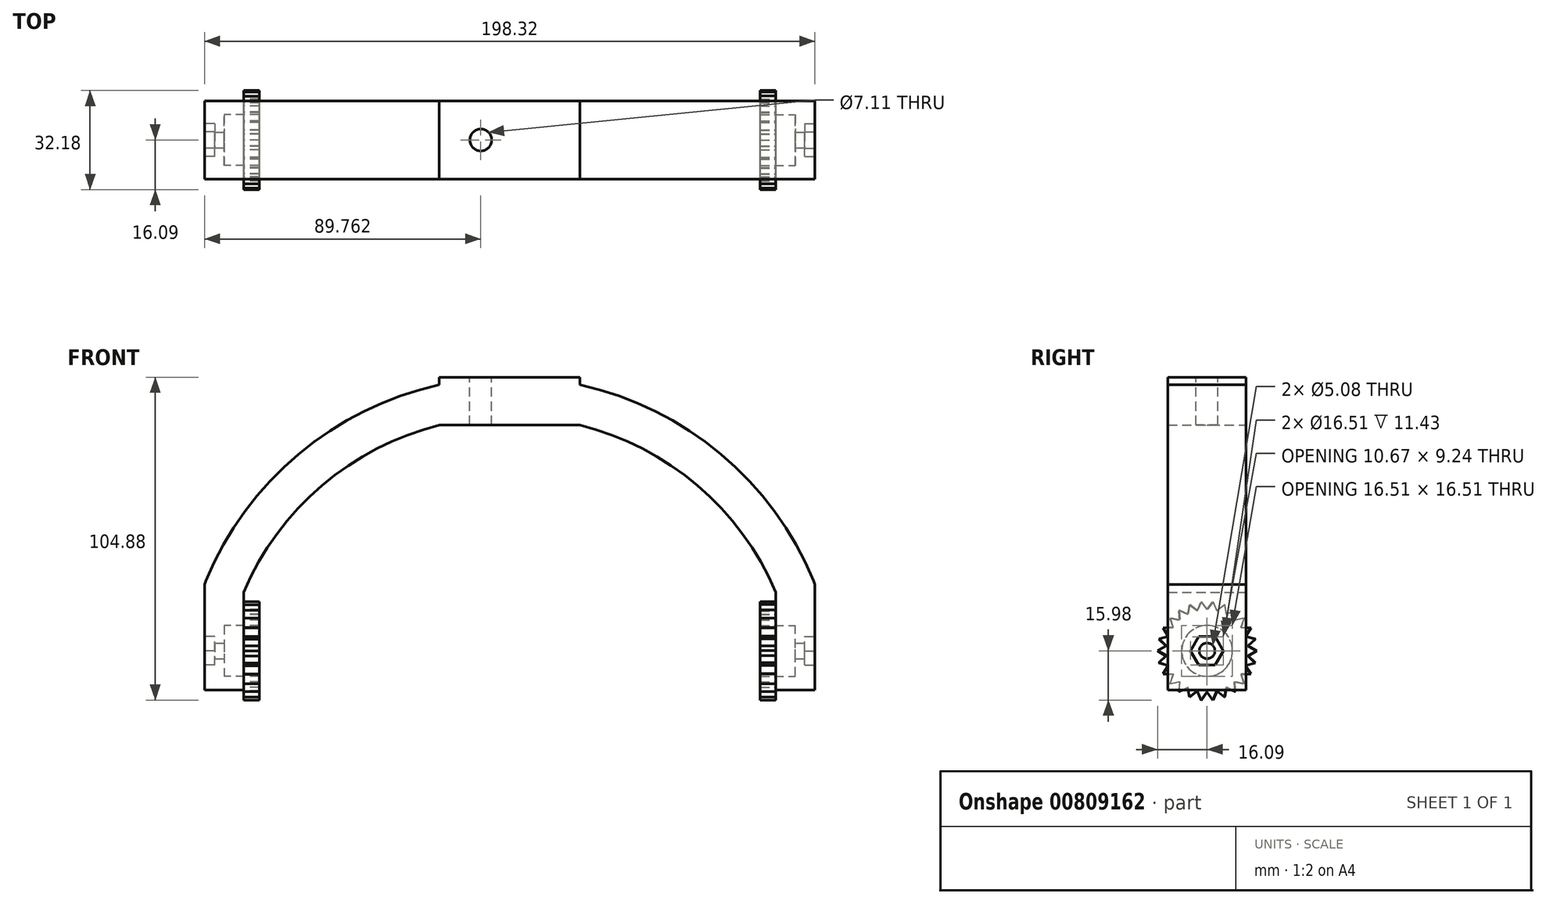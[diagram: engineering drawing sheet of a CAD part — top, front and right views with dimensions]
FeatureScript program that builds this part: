
annotation { "Feature Type Name" : "Feature", "Feature Type Description" : "" }
export const myFeature = defineFeature(function(context is Context, id is Id, definition is map)
    precondition{}
    {
        {
            var Q0;
            Q0=qCreatedBy(makeId("Front.planeOp"),FACE);
            var sketch = newSketch(context, id + "F0", { "sketchPlane" : qUnion([Q0])});
            skArc(sketch, "E0", {"start": v(92.81, 33.02) * mm, "mid": v(0, 95.25) * mm, "end": v(-92.81, 33.02) * mm});
            skLineSegment(sketch, "E1", {"start": v(-92.81, 33.02) * mm, "end": v(-92.81, 0) * mm});
            skLineSegment(sketch, "E2", {"start": v(92.81, 33.02) * mm, "end": v(92.81, 0) * mm});
            skLineSegment(sketch, "E3", {"start": v(0, 0) * mm, "end": v(0, 95.25) * mm, "construction": true});
            skSolve(sketch);
        }
        {
            var Q0;
            Q0=qCreatedBy(makeId("Top.planeOp"),FACE);
            var sketch = newSketch(context, id + "F1", { "sketchPlane" : qUnion([Q0])});
            skPoint(sketch, "E4.0", {"position": v(-92.81, 0) * mm});
            skLineSegment(sketch, "E5.bottom", {"start": v(-99.16, 12.7) * mm, "end": v(-86.46, 12.7) * mm});
            skLineSegment(sketch, "E5.top", {"start": v(-99.16, -12.7) * mm, "end": v(-86.46, -12.7) * mm});
            skLineSegment(sketch, "E5.left", {"start": v(-99.16, 12.7) * mm, "end": v(-99.16, -12.7) * mm});
            skLineSegment(sketch, "E5.right", {"start": v(-86.46, 12.7) * mm, "end": v(-86.46, -12.7) * mm});
            skSolve(sketch);
        }
        {
            var Q0;
            Q0=qSketchRegion(id+"F1",true);
            var Q1;
            Q1=qConstructionFilter(qBodyType(qCreatedBy(id+"F0",EDGE),BodyType.WIRE),ConstructionObject.NO);
            sweep(context, id + "F2", {"profiles" : qUnion([Q0]), "path" : qUnion([Q1])});
        }
        {
            var Q0;
            Q0=qCreatedBy(makeId("Right.planeOp"),FACE);
            var sketch = newSketch(context, id + "F3", { "sketchPlane" : qUnion([Q0])});
            skCircle(sketch, "E6", {"center": v(0, 12.7) * mm, "radius": 2.54 * mm});
            skSolve(sketch);
        }
        {
            var Q0;
            Q0=qSketchRegion(id+"F3",true);
            extrude(context, id + "F4", {"entities" : qUnion([Q0]), "operationType" : NewBodyOperationType.REMOVE, "endBound" : BoundingType.SYMMETRIC, "oppositeDirection" : true, "depth" : 254 * mm, "offsetDistance" : 25.4 * mm});
        }
        {
            var Q0;
            Q0=makeQuery(id+"F2.opSweep","SWEPT_FACE",FACE,{"disambiguationData":[OSD([sQuery(id+"F0.wireOp",EDGE,"E2"),sQuery(id+"F1.wireOp",EDGE,"E5.left")])]});
            var Q1;
            Q1=makeQuery(id+"F2.opSweep","CAP_VERTEX",VERTEX,{"disambiguationData":[OSD([sQuery(id+"F0.wireOp",EDGE,"E2"),sQuery(id+"F1.wireOp",EDGE,"E5.bottom"),sQuery(id+"F1.wireOp",EDGE,"E5.left")])],"isStart":false});
            cPlane(context, id + "F5", {"entities" : qUnion([Q0, Q1]), "cplaneType" : CPlaneType.PLANE_POINT, "offset" : 25.4 * mm, "width" : 152.4 * mm, "height" : 152.4 * mm});
        }
        {
            var Q0;
            Q0=qCreatedBy(id+"F5.planeOp",FACE);
            var sketch = newSketch(context, id + "F6", { "sketchPlane" : qUnion([Q0])});
            skCircle(sketch, "E7", {"center": v(0, 12.7) * mm, "radius": 5.33 * mm, "construction": true});
            skLineSegment(sketch, "E8.0", {"start": v(-2.67, 17.32) * mm, "end": v(2.67, 17.32) * mm});
            skLineSegment(sketch, "E8.1", {"start": v(2.67, 17.32) * mm, "end": v(5.33, 12.7) * mm});
            skLineSegment(sketch, "E8.2", {"start": v(5.33, 12.7) * mm, "end": v(2.67, 8.08) * mm});
            skLineSegment(sketch, "E8.3", {"start": v(2.67, 8.08) * mm, "end": v(-2.67, 8.08) * mm});
            skLineSegment(sketch, "E8.4", {"start": v(-2.67, 8.08) * mm, "end": v(-5.33, 12.7) * mm});
            skLineSegment(sketch, "E8.5", {"start": v(-5.33, 12.7) * mm, "end": v(-2.67, 17.32) * mm});
            skSolve(sketch);
        }
        {
            var Q0;
            Q0=makeQuery(id+"F6.imprint","IMPRINT",FACE,{"disambiguationData":[TD([[makeQuery(id+"F6.imprint","IMPRINT",EDGE,{"derivedFrom":sQuery(id+"F6.wireOp",EDGE,"E8.0")}),-1.0]])]});
            extrude(context, id + "F7", {"entities" : qUnion([Q0]), "operationType" : NewBodyOperationType.REMOVE, "oppositeDirection" : true, "depth" : 3.3 * mm, "offsetDistance" : 25.4 * mm});
        }
        {
            var Q0;
            Q0=makeQuery(id+"F2.opSweep","SWEPT_FACE",FACE,{"disambiguationData":[OSD([sQuery(id+"F0.wireOp",EDGE,"E1"),sQuery(id+"F1.wireOp",EDGE,"E5.left")])]});
            var Q1;
            Q1=makeQuery(id+"F2.opSweep","CAP_VERTEX",VERTEX,{"disambiguationData":[OSD([sQuery(id+"F0.wireOp",EDGE,"E1"),sQuery(id+"F1.wireOp",EDGE,"E5.bottom"),sQuery(id+"F1.wireOp",EDGE,"E5.left")])],"isStart":true});
            cPlane(context, id + "F8", {"entities" : qUnion([Q0, Q1]), "cplaneType" : CPlaneType.PLANE_POINT, "offset" : 25.4 * mm, "width" : 152.4 * mm, "height" : 152.4 * mm});
        }
        {
            var Q0;
            Q0=qCreatedBy(id+"F8.planeOp",FACE);
            var sketch = newSketch(context, id + "F9", { "sketchPlane" : qUnion([Q0])});
            skLineSegment(sketch, "E9", {"start": v(0, 0) * mm, "end": v(0, 12.7) * mm, "construction": true});
            skCircle(sketch, "E10", {"center": v(0, 12.7) * mm, "radius": 5.33 * mm, "construction": true});
            skLineSegment(sketch, "E11.0", {"start": v(-2.67, 17.32) * mm, "end": v(2.67, 17.32) * mm});
            skLineSegment(sketch, "E11.1", {"start": v(2.67, 17.32) * mm, "end": v(5.33, 12.7) * mm});
            skLineSegment(sketch, "E11.2", {"start": v(5.33, 12.7) * mm, "end": v(2.67, 8.08) * mm});
            skLineSegment(sketch, "E11.3", {"start": v(2.67, 8.08) * mm, "end": v(-2.67, 8.08) * mm});
            skLineSegment(sketch, "E11.4", {"start": v(-2.67, 8.08) * mm, "end": v(-5.33, 12.7) * mm});
            skLineSegment(sketch, "E11.5", {"start": v(-5.33, 12.7) * mm, "end": v(-2.67, 17.32) * mm});
            skSolve(sketch);
        }
        {
            var Q0;
            Q0=makeQuery(id+"F9.imprint","IMPRINT",FACE,{"disambiguationData":[TD([[makeQuery(id+"F9.imprint","IMPRINT",EDGE,{"derivedFrom":sQuery(id+"F9.wireOp",EDGE,"E11.0")}),-1.0]])]});
            extrude(context, id + "F10", {"entities" : qUnion([Q0]), "operationType" : NewBodyOperationType.REMOVE, "oppositeDirection" : true, "depth" : 3.3 * mm, "offsetDistance" : 25.4 * mm});
        }
        {
            var Q0;
            Q0=makeQuery(id+"F2.opSweep","SWEPT_FACE",FACE,{"disambiguationData":[OSD([sQuery(id+"F0.wireOp",EDGE,"E1"),sQuery(id+"F1.wireOp",EDGE,"E5.left")])]});
            cPlane(context, id + "F11", {"entities" : qUnion([Q0]), "cplaneType" : CPlaneType.OFFSET, "offset" : 6.35 * mm, "oppositeDirection" : true, "width" : 152.4 * mm, "height" : 152.4 * mm});
        }
        {
            var Q0;
            Q0=qCreatedBy(id+"F11.planeOp",FACE);
            var sketch = newSketch(context, id + "F12", { "sketchPlane" : qUnion([Q0])});
            skLineSegment(sketch, "E12", {"start": v(0, 0) * mm, "end": v(0, 12.7) * mm, "construction": true});
            skCircle(sketch, "E13", {"center": v(0, 12.7) * mm, "radius": 8.26 * mm});
            skSolve(sketch);
        }
        {
            var Q0;
            Q0=makeQuery(id+"F2.opSweep","SWEPT_FACE",FACE,{"disambiguationData":[OSD([sQuery(id+"F0.wireOp",EDGE,"E2"),sQuery(id+"F1.wireOp",EDGE,"E5.left")])]});
            cPlane(context, id + "F13", {"entities" : qUnion([Q0]), "cplaneType" : CPlaneType.OFFSET, "offset" : 6.35 * mm, "oppositeDirection" : true, "width" : 152.4 * mm, "height" : 152.4 * mm});
        }
        {
            var Q0;
            Q0=qCreatedBy(id+"F13.planeOp",FACE);
            var sketch = newSketch(context, id + "F14", { "sketchPlane" : qUnion([Q0])});
            skLineSegment(sketch, "E14", {"start": v(0, 0) * mm, "end": v(0, 12.7) * mm, "construction": true});
            skCircle(sketch, "E15", {"center": v(0, 12.7) * mm, "radius": 8.26 * mm});
            skSolve(sketch);
        }
        {
            var Q0;
            Q0=makeQuery(id+"F2.opSweep","SWEPT_FACE",FACE,{"disambiguationData":[OSD([sQuery(id+"F0.wireOp",EDGE,"E1"),sQuery(id+"F1.wireOp",EDGE,"E5.right")])]});
            var sketch = newSketch(context, id + "F15", { "sketchPlane" : qUnion([Q0])});
            skCircle(sketch, "E16", {"center": v(0, 12.7) * mm, "radius": 13.34 * mm, "construction": true});
            skLineSegment(sketch, "E17", {"start": v(-3.28, 25.63) * mm, "end": v(-2, 28.67) * mm});
            skLineSegment(sketch, "E18", {"start": v(-2, 28.67) * mm, "end": v(0, 26.04) * mm});
            skLineSegment(sketch, "E19.1.0", {"start": v(-6.27, 24.47) * mm, "end": v(-5.76, 27.73) * mm});
            skLineSegment(sketch, "E19.1.1", {"start": v(-5.76, 27.73) * mm, "end": v(-3.2, 25.65) * mm});
            skLineSegment(sketch, "E19.2.0", {"start": v(-8.9, 22.62) * mm, "end": v(-9.18, 25.91) * mm});
            skLineSegment(sketch, "E19.2.1", {"start": v(-9.18, 25.91) * mm, "end": v(-6.2, 24.5) * mm});
            skLineSegment(sketch, "E19.3.0", {"start": v(-11.02, 20.2) * mm, "end": v(-12.08, 23.33) * mm});
            skLineSegment(sketch, "E19.3.1", {"start": v(-12.08, 23.33) * mm, "end": v(-8.84, 22.68) * mm});
            skLineSegment(sketch, "E19.4.0", {"start": v(-12.5, 17.35) * mm, "end": v(-14.27, 20.13) * mm});
            skLineSegment(sketch, "E19.4.1", {"start": v(-14.27, 20.13) * mm, "end": v(-10.97, 20.28) * mm});
            skLineSegment(sketch, "E19.5.0", {"start": v(-13.25, 14.22) * mm, "end": v(-15.64, 16.5) * mm});
            skLineSegment(sketch, "E19.5.1", {"start": v(-15.64, 16.5) * mm, "end": v(-12.47, 17.43) * mm});
            skLineSegment(sketch, "E19.6.0", {"start": v(-13.23, 11) * mm, "end": v(-16.1, 12.65) * mm});
            skLineSegment(sketch, "E19.6.1", {"start": v(-16.1, 12.65) * mm, "end": v(-13.24, 14.3) * mm});
            skLineSegment(sketch, "E19.7.0", {"start": v(-12.44, 7.89) * mm, "end": v(-15.61, 8.8) * mm});
            skLineSegment(sketch, "E19.7.1", {"start": v(-15.61, 8.8) * mm, "end": v(-13.24, 11.1) * mm});
            skLineSegment(sketch, "E19.8.0", {"start": v(-10.92, 5.05) * mm, "end": v(-14.22, 5.17) * mm});
            skLineSegment(sketch, "E19.8.1", {"start": v(-14.22, 5.17) * mm, "end": v(-12.47, 7.97) * mm});
            skLineSegment(sketch, "E19.9.0", {"start": v(-8.78, 2.66) * mm, "end": v(-12, 1.99) * mm});
            skLineSegment(sketch, "E19.9.1", {"start": v(-12, 1.99) * mm, "end": v(-10.97, 5.12) * mm});
            skLineSegment(sketch, "E19.10.0", {"start": v(-6.12, 0.85) * mm, "end": v(-9.1, -0.57) * mm});
            skLineSegment(sketch, "E19.10.1", {"start": v(-9.1, -0.57) * mm, "end": v(-8.84, 2.72) * mm});
            skLineSegment(sketch, "E19.11.0", {"start": v(-3.1, -0.27) * mm, "end": v(-5.66, -2.37) * mm});
            skLineSegment(sketch, "E19.11.1", {"start": v(-5.66, -2.37) * mm, "end": v(-6.2, 0.9) * mm});
            skLineSegment(sketch, "E19.12.0", {"start": v(0.09, -0.63) * mm, "end": v(-1.89, -3.28) * mm});
            skLineSegment(sketch, "E19.12.1", {"start": v(-1.89, -3.28) * mm, "end": v(-3.2, -0.25) * mm});
            skLineSegment(sketch, "E19.13.0", {"start": v(3.28, -0.23) * mm, "end": v(2, -3.27) * mm});
            skLineSegment(sketch, "E19.13.1", {"start": v(2, -3.27) * mm, "end": v(0, -0.63) * mm});
            skLineSegment(sketch, "E19.14.0", {"start": v(6.27, 0.93) * mm, "end": v(5.76, -2.33) * mm});
            skLineSegment(sketch, "E19.14.1", {"start": v(5.76, -2.33) * mm, "end": v(3.2, -0.25) * mm});
            skLineSegment(sketch, "E19.15.0", {"start": v(8.9, 2.78) * mm, "end": v(9.18, -0.51) * mm});
            skLineSegment(sketch, "E19.15.1", {"start": v(9.18, -0.51) * mm, "end": v(6.2, 0.9) * mm});
            skLineSegment(sketch, "E19.16.0", {"start": v(11.02, 5.2) * mm, "end": v(12.08, 2.07) * mm});
            skLineSegment(sketch, "E19.16.1", {"start": v(12.08, 2.07) * mm, "end": v(8.84, 2.72) * mm});
            skLineSegment(sketch, "E19.17.0", {"start": v(12.5, 8.05) * mm, "end": v(14.27, 5.27) * mm});
            skLineSegment(sketch, "E19.17.1", {"start": v(14.27, 5.27) * mm, "end": v(10.97, 5.12) * mm});
            skLineSegment(sketch, "E19.18.0", {"start": v(13.25, 11.18) * mm, "end": v(15.64, 8.9) * mm});
            skLineSegment(sketch, "E19.18.1", {"start": v(15.64, 8.9) * mm, "end": v(12.47, 7.97) * mm});
            skLineSegment(sketch, "E19.19.0", {"start": v(13.23, 14.4) * mm, "end": v(16.1, 12.75) * mm});
            skLineSegment(sketch, "E19.19.1", {"start": v(16.1, 12.75) * mm, "end": v(13.24, 11.1) * mm});
            skLineSegment(sketch, "E19.20.0", {"start": v(12.44, 17.51) * mm, "end": v(15.61, 16.6) * mm});
            skLineSegment(sketch, "E19.20.1", {"start": v(15.61, 16.6) * mm, "end": v(13.24, 14.3) * mm});
            skLineSegment(sketch, "E19.21.0", {"start": v(10.92, 20.35) * mm, "end": v(14.22, 20.23) * mm});
            skLineSegment(sketch, "E19.21.1", {"start": v(14.22, 20.23) * mm, "end": v(12.47, 17.43) * mm});
            skLineSegment(sketch, "E19.22.0", {"start": v(8.78, 22.74) * mm, "end": v(12, 23.41) * mm});
            skLineSegment(sketch, "E19.22.1", {"start": v(12, 23.41) * mm, "end": v(10.97, 20.28) * mm});
            skLineSegment(sketch, "E19.23.0", {"start": v(6.12, 24.55) * mm, "end": v(9.1, 25.97) * mm});
            skLineSegment(sketch, "E19.23.1", {"start": v(9.1, 25.97) * mm, "end": v(8.84, 22.68) * mm});
            skLineSegment(sketch, "E19.24.0", {"start": v(3.1, 25.67) * mm, "end": v(5.66, 27.77) * mm});
            skLineSegment(sketch, "E19.24.1", {"start": v(5.66, 27.77) * mm, "end": v(6.2, 24.5) * mm});
            skLineSegment(sketch, "E19.25.0", {"start": v(-0.09, 26.03) * mm, "end": v(1.89, 28.68) * mm});
            skLineSegment(sketch, "E19.25.1", {"start": v(1.89, 28.68) * mm, "end": v(3.2, 25.65) * mm});
            skSolve(sketch);
        }
        {
            var Q0;
            Q0=qSketchRegion(id+"F15",true);
            extrude(context, id + "F16", {"entities" : qUnion([Q0]), "operationType" : NewBodyOperationType.ADD, "depth" : 5.08 * mm, "offsetDistance" : 25.4 * mm});
        }
        {
            var Q0;
            Q0=makeQuery(id+"F2.opSweep","SWEPT_FACE",FACE,{"disambiguationData":[OSD([sQuery(id+"F0.wireOp",EDGE,"E2"),sQuery(id+"F1.wireOp",EDGE,"E5.right")])]});
            var sketch = newSketch(context, id + "F17", { "sketchPlane" : qUnion([Q0])});
            skCircle(sketch, "E20", {"center": v(0, 12.7) * mm, "radius": 13.34 * mm, "construction": true});
            skLineSegment(sketch, "E21", {"start": v(-3.28, 25.63) * mm, "end": v(-2, 28.67) * mm});
            skLineSegment(sketch, "E22", {"start": v(-2, 28.67) * mm, "end": v(0, 26.04) * mm});
            skLineSegment(sketch, "E23.1.0", {"start": v(-5.76, 27.73) * mm, "end": v(-3.2, 25.65) * mm});
            skLineSegment(sketch, "E23.1.1", {"start": v(-6.27, 24.47) * mm, "end": v(-5.76, 27.73) * mm});
            skLineSegment(sketch, "E23.2.0", {"start": v(-9.18, 25.91) * mm, "end": v(-6.2, 24.5) * mm});
            skLineSegment(sketch, "E23.2.1", {"start": v(-8.9, 22.62) * mm, "end": v(-9.18, 25.91) * mm});
            skLineSegment(sketch, "E23.3.0", {"start": v(-12.08, 23.33) * mm, "end": v(-8.84, 22.68) * mm});
            skLineSegment(sketch, "E23.3.1", {"start": v(-11.02, 20.2) * mm, "end": v(-12.08, 23.33) * mm});
            skLineSegment(sketch, "E23.4.0", {"start": v(-14.27, 20.13) * mm, "end": v(-10.97, 20.28) * mm});
            skLineSegment(sketch, "E23.4.1", {"start": v(-12.5, 17.35) * mm, "end": v(-14.27, 20.13) * mm});
            skLineSegment(sketch, "E23.5.0", {"start": v(-15.64, 16.5) * mm, "end": v(-12.47, 17.43) * mm});
            skLineSegment(sketch, "E23.5.1", {"start": v(-13.25, 14.22) * mm, "end": v(-15.64, 16.5) * mm});
            skLineSegment(sketch, "E23.6.0", {"start": v(-16.1, 12.65) * mm, "end": v(-13.24, 14.3) * mm});
            skLineSegment(sketch, "E23.6.1", {"start": v(-13.23, 11) * mm, "end": v(-16.1, 12.65) * mm});
            skLineSegment(sketch, "E23.7.0", {"start": v(-15.61, 8.8) * mm, "end": v(-13.24, 11.1) * mm});
            skLineSegment(sketch, "E23.7.1", {"start": v(-12.44, 7.89) * mm, "end": v(-15.61, 8.8) * mm});
            skLineSegment(sketch, "E23.8.0", {"start": v(-14.22, 5.17) * mm, "end": v(-12.47, 7.97) * mm});
            skLineSegment(sketch, "E23.8.1", {"start": v(-10.92, 5.05) * mm, "end": v(-14.22, 5.17) * mm});
            skLineSegment(sketch, "E23.9.0", {"start": v(-12, 1.99) * mm, "end": v(-10.97, 5.12) * mm});
            skLineSegment(sketch, "E23.9.1", {"start": v(-8.78, 2.66) * mm, "end": v(-12, 1.99) * mm});
            skLineSegment(sketch, "E23.10.0", {"start": v(-9.1, -0.57) * mm, "end": v(-8.84, 2.72) * mm});
            skLineSegment(sketch, "E23.10.1", {"start": v(-6.12, 0.85) * mm, "end": v(-9.1, -0.57) * mm});
            skLineSegment(sketch, "E23.11.0", {"start": v(-5.66, -2.37) * mm, "end": v(-6.2, 0.9) * mm});
            skLineSegment(sketch, "E23.11.1", {"start": v(-3.1, -0.27) * mm, "end": v(-5.66, -2.37) * mm});
            skLineSegment(sketch, "E23.12.0", {"start": v(-1.89, -3.28) * mm, "end": v(-3.2, -0.25) * mm});
            skLineSegment(sketch, "E23.12.1", {"start": v(0.09, -0.63) * mm, "end": v(-1.89, -3.28) * mm});
            skLineSegment(sketch, "E23.13.0", {"start": v(2, -3.27) * mm, "end": v(0, -0.63) * mm});
            skLineSegment(sketch, "E23.13.1", {"start": v(3.28, -0.23) * mm, "end": v(2, -3.27) * mm});
            skLineSegment(sketch, "E23.14.0", {"start": v(5.76, -2.33) * mm, "end": v(3.2, -0.25) * mm});
            skLineSegment(sketch, "E23.14.1", {"start": v(6.27, 0.93) * mm, "end": v(5.76, -2.33) * mm});
            skLineSegment(sketch, "E23.15.0", {"start": v(9.18, -0.51) * mm, "end": v(6.2, 0.9) * mm});
            skLineSegment(sketch, "E23.15.1", {"start": v(8.9, 2.78) * mm, "end": v(9.18, -0.51) * mm});
            skLineSegment(sketch, "E23.16.0", {"start": v(12.08, 2.07) * mm, "end": v(8.84, 2.72) * mm});
            skLineSegment(sketch, "E23.16.1", {"start": v(11.02, 5.2) * mm, "end": v(12.08, 2.07) * mm});
            skLineSegment(sketch, "E23.17.0", {"start": v(14.27, 5.27) * mm, "end": v(10.97, 5.12) * mm});
            skLineSegment(sketch, "E23.17.1", {"start": v(12.5, 8.05) * mm, "end": v(14.27, 5.27) * mm});
            skLineSegment(sketch, "E23.18.0", {"start": v(15.64, 8.9) * mm, "end": v(12.47, 7.97) * mm});
            skLineSegment(sketch, "E23.18.1", {"start": v(13.25, 11.18) * mm, "end": v(15.64, 8.9) * mm});
            skLineSegment(sketch, "E23.19.0", {"start": v(16.1, 12.75) * mm, "end": v(13.24, 11.1) * mm});
            skLineSegment(sketch, "E23.19.1", {"start": v(13.23, 14.4) * mm, "end": v(16.1, 12.75) * mm});
            skLineSegment(sketch, "E23.20.0", {"start": v(15.61, 16.6) * mm, "end": v(13.24, 14.3) * mm});
            skLineSegment(sketch, "E23.20.1", {"start": v(12.44, 17.51) * mm, "end": v(15.61, 16.6) * mm});
            skLineSegment(sketch, "E23.21.0", {"start": v(14.22, 20.23) * mm, "end": v(12.47, 17.43) * mm});
            skLineSegment(sketch, "E23.21.1", {"start": v(10.92, 20.35) * mm, "end": v(14.22, 20.23) * mm});
            skLineSegment(sketch, "E23.22.0", {"start": v(12, 23.41) * mm, "end": v(10.97, 20.28) * mm});
            skLineSegment(sketch, "E23.22.1", {"start": v(8.78, 22.74) * mm, "end": v(12, 23.41) * mm});
            skLineSegment(sketch, "E23.23.0", {"start": v(9.1, 25.97) * mm, "end": v(8.84, 22.68) * mm});
            skLineSegment(sketch, "E23.23.1", {"start": v(6.12, 24.55) * mm, "end": v(9.1, 25.97) * mm});
            skLineSegment(sketch, "E23.24.0", {"start": v(5.66, 27.77) * mm, "end": v(6.2, 24.5) * mm});
            skLineSegment(sketch, "E23.24.1", {"start": v(3.1, 25.67) * mm, "end": v(5.66, 27.77) * mm});
            skLineSegment(sketch, "E23.25.0", {"start": v(1.89, 28.68) * mm, "end": v(3.2, 25.65) * mm});
            skLineSegment(sketch, "E23.25.1", {"start": v(-0.09, 26.03) * mm, "end": v(1.89, 28.68) * mm});
            skSolve(sketch);
        }
        {
            var Q0;
            Q0=qSketchRegion(id+"F17",true);
            var Q1;
            Q1=makeQuery(id+"F2.opSweep","SWEPT_FACE",FACE,{"disambiguationData":[OSD([sQuery(id+"F0.wireOp",EDGE,"E2"),sQuery(id+"F1.wireOp",EDGE,"E5.left")])]});
            extrude(context, id + "F18", {"entities" : qUnion([Q0, Q1]), "operationType" : NewBodyOperationType.ADD, "depth" : 5.08 * mm, "offsetDistance" : 25.4 * mm});
        }
        {
            var Q0;
            Q0=qSketchRegion(id+"F12",true);
            extrude(context, id + "F19", {"entities" : qUnion([Q0]), "operationType" : NewBodyOperationType.REMOVE, "oppositeDirection" : true, "depth" : 63.75 * mm, "offsetDistance" : 25.4 * mm});
        }
        {
            var Q0;
            Q0=qSketchRegion(id+"F14",true);
            extrude(context, id + "F20", {"entities" : qUnion([Q0]), "operationType" : NewBodyOperationType.REMOVE, "oppositeDirection" : true, "depth" : 25.4 * mm, "offsetDistance" : 25.4 * mm});
        }
        {
            var Q0;
            Q0=makeQuery(id+"F2.opSweep","SWEPT_EDGE",EDGE,{"disambiguationData":[OSD([sQuery(id+"F0.wireOp",EDGE,"E0"),sQuery(id+"F1.wireOp",EDGE,"E5.top"),sQuery(id+"F1.wireOp",EDGE,"E5.left")]),OD(2.0)]});
            cPoint(context, id + "F21", {"entities" : qUnion([Q0]), "parameter" : 0.5});
        }
        {
            var Q0;
            Q0=qCreatedBy(makeId("Top.planeOp"),FACE);
            var Q1;
            Q1=qCreatedBy(id+"F21",VERTEX);
            cPlane(context, id + "F22", {"entities" : qUnion([Q0, Q1]), "cplaneType" : CPlaneType.PLANE_POINT, "offset" : 25.4 * mm, "width" : 152.4 * mm, "height" : 152.4 * mm});
        }
        {
            var Q0;
            Q0=qCreatedBy(id+"F22.planeOp",FACE);
            var sketch = newSketch(context, id + "F23", { "sketchPlane" : qUnion([Q0])});
            skFitSpline(sketch, "E24.0", {"points": [v(-103.2, 12.7) * mm, v(-34.4, 12.7) * mm, v(34.4, 12.7) * mm, v(103.2, 12.7) * mm]});
            skLineSegment(sketch, "E25.bottom", {"start": v(-22.86, 12.7) * mm, "end": v(22.86, 12.7) * mm});
            skLineSegment(sketch, "E25.top", {"start": v(-22.86, -12.7) * mm, "end": v(22.86, -12.7) * mm});
            skLineSegment(sketch, "E25.left", {"start": v(-22.86, 12.7) * mm, "end": v(-22.86, -12.7) * mm});
            skLineSegment(sketch, "E25.right", {"start": v(22.86, 12.7) * mm, "end": v(22.86, -12.7) * mm});
            skPoint(sketch, "E25.middle", {"position": v(0, 0) * mm});
            skSolve(sketch);
        }
        {
            var Q0;
            Q0=qSketchRegion(id+"F23",true);
            extrude(context, id + "F24", {"entities" : qUnion([Q0]), "operationType" : NewBodyOperationType.ADD, "oppositeDirection" : true, "depth" : 15.5 * mm, "offsetDistance" : 25.4 * mm});
        }
        {
            var Q0;
            Q0=qCreatedBy(id+"F22.planeOp",FACE);
            var sketch = newSketch(context, id + "F25", { "sketchPlane" : qUnion([Q0])});
            skCircle(sketch, "E26", {"center": v(-9.4, 0) * mm, "radius": 3.56 * mm});
            skCircle(sketch, "E27.MirrorC", {"center": v(9.4, 0) * mm, "radius": 3.56 * mm});
            skSolve(sketch);
        }
        {
            var Q0;
            Q0=makeQuery(id+"F25.imprint","IMPRINT",FACE,{"disambiguationData":[TD([[makeQuery(id+"F25.imprint","IMPRINT",EDGE,{"derivedFrom":sQuery(id+"F25.wireOp",EDGE,"E26")}),1.0]])]});
            var Q1;
            Q1=makeQuery(id+"F25.imprint","IMPRINT",FACE,{"disambiguationData":[TD([[makeQuery(id+"F25.imprint","IMPRINT",EDGE,{"derivedFrom":sQuery(id+"F25.wireOp",EDGE,"E27.MirrorC")}),-1.0]])]});
            extrude(context, id + "F26", {"entities" : qUnion([Q0, Q1]), "operationType" : NewBodyOperationType.REMOVE, "oppositeDirection" : true, "depth" : 25.4 * mm, "offsetDistance" : 25.4 * mm});
        }
    });
